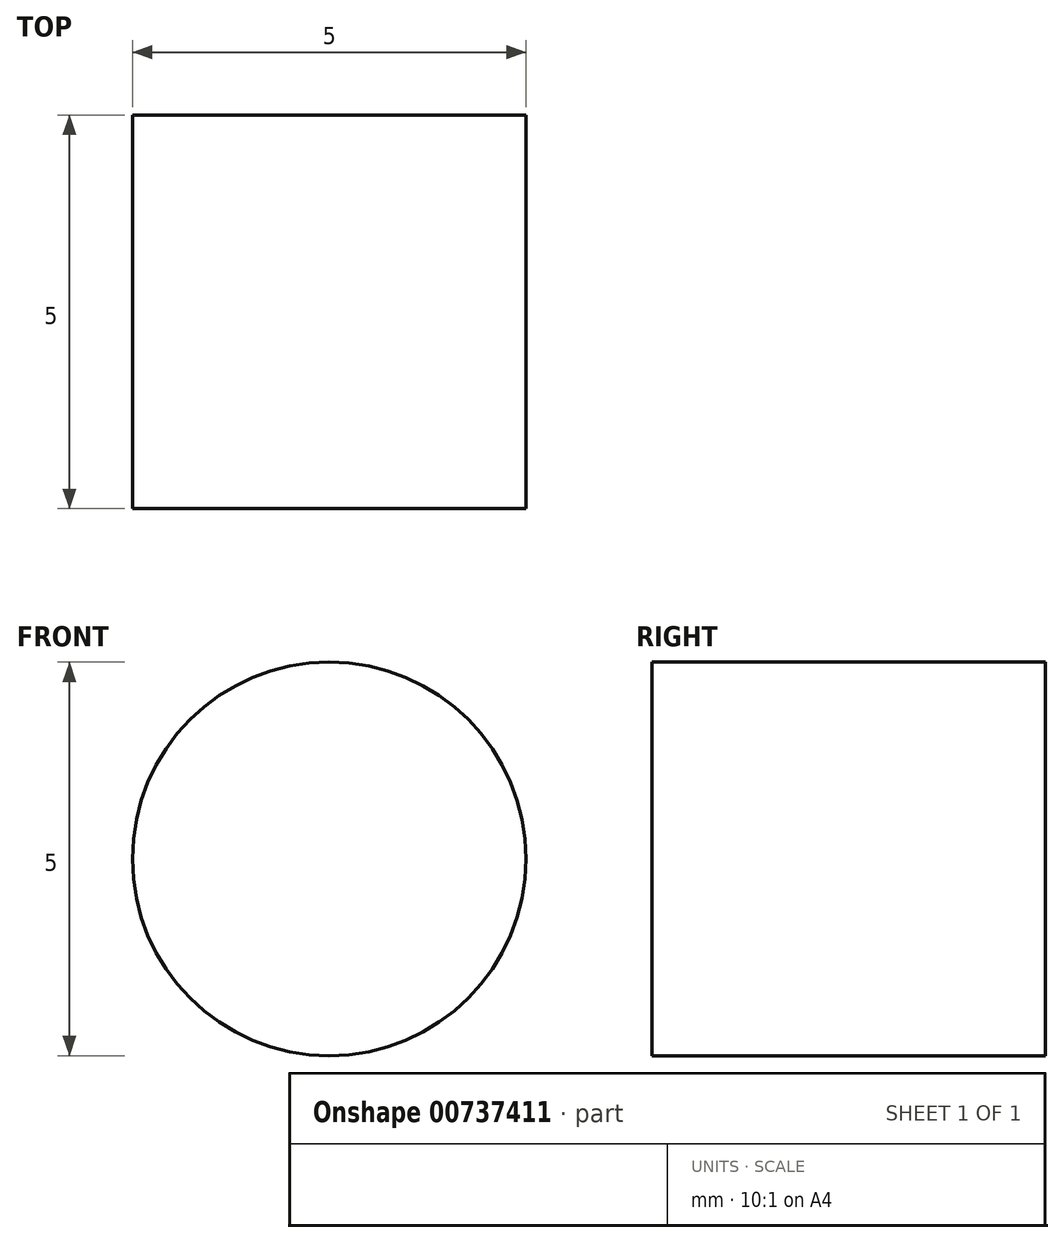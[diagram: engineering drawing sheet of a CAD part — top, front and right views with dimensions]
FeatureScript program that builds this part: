
annotation { "Feature Type Name" : "Feature", "Feature Type Description" : "" }
export const myFeature = defineFeature(function(context is Context, id is Id, definition is map)
    precondition{}
    {
        {
            var Q0;
            Q0=qCreatedBy(makeId("Front.planeOp"),FACE);
            var sketch = newSketch(context, id + "F0", { "sketchPlane" : qUnion([Q0])});
            skCircle(sketch, "E0", {"center": v(0, 0) * mm, "radius": 2.5 * mm});
            skSolve(sketch);
        }
        {
            var Q0;
            Q0=makeQuery(id+"F0.imprint","IMPRINT",FACE,{"disambiguationData":[TD([[makeQuery(id+"F0.imprint","IMPRINT",EDGE,{"derivedFrom":sQuery(id+"F0.wireOp",EDGE,"E0")}),1.0]])]});
            extrude(context, id + "F1", {"entities" : qUnion([Q0]), "depth" : 5 * mm, "offsetDistance" : 25 * mm});
        }
    });
